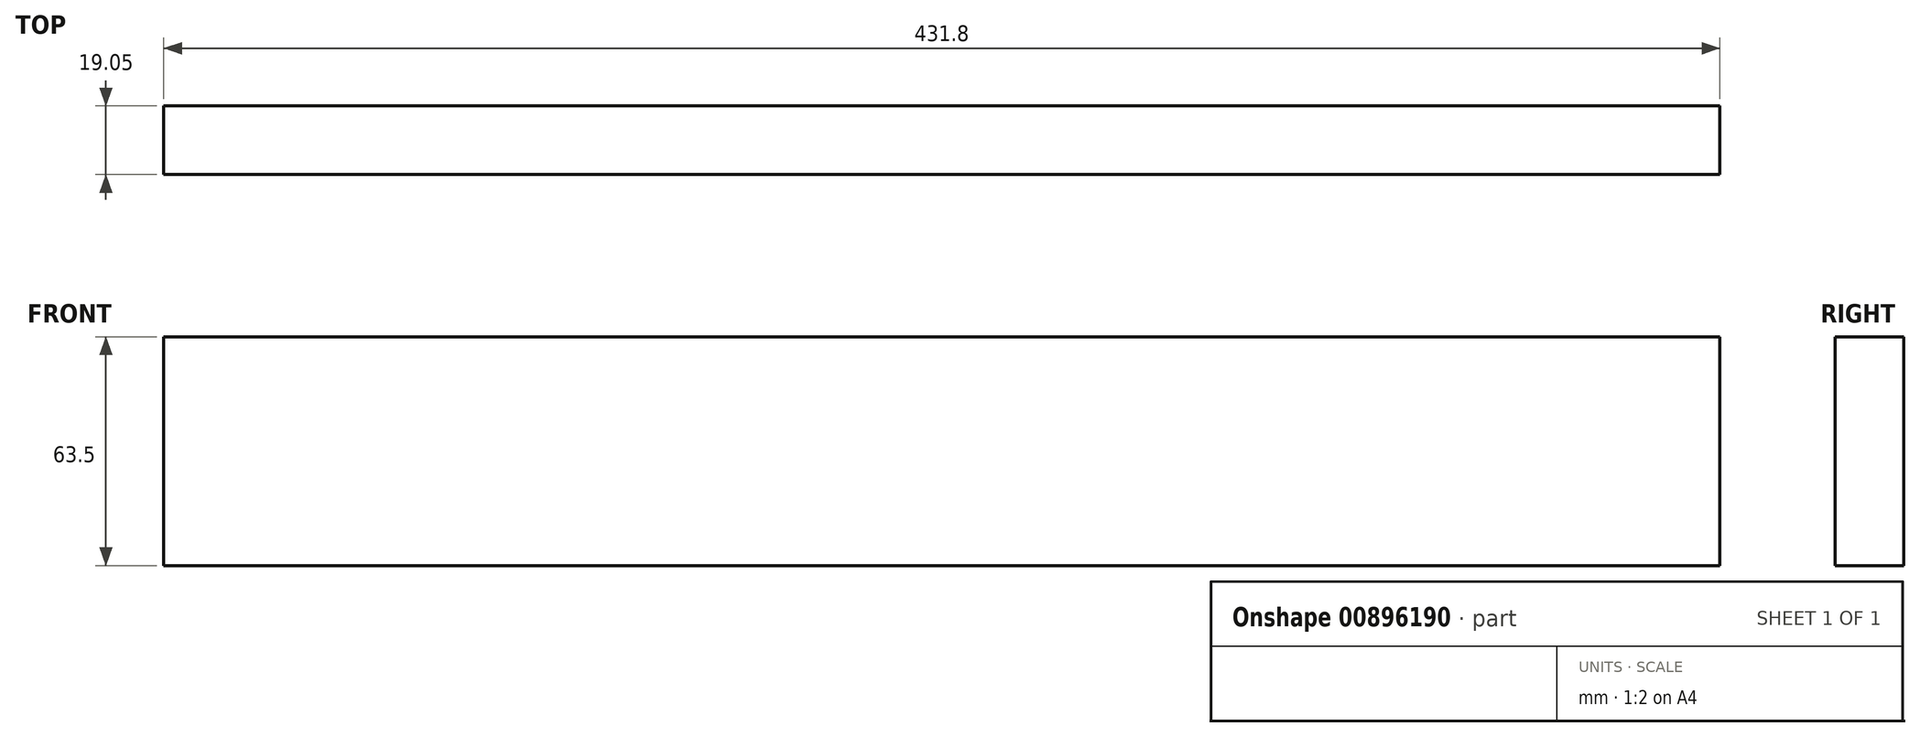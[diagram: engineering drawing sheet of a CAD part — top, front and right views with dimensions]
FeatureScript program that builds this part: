
annotation { "Feature Type Name" : "Feature", "Feature Type Description" : "" }
export const myFeature = defineFeature(function(context is Context, id is Id, definition is map)
    precondition{}
    {
        {
            var Q0;
            Q0=qCreatedBy(makeId("Front.planeOp"),FACE);
            var sketch = newSketch(context, id + "F0", { "sketchPlane" : qUnion([Q0])});
            skLineSegment(sketch, "E0.bottom", {"start": v(0, 0) * mm, "end": v(431.8, 0) * mm});
            skLineSegment(sketch, "E0.top", {"start": v(0, -63.5) * mm, "end": v(431.8, -63.5) * mm});
            skLineSegment(sketch, "E0.left", {"start": v(0, 0) * mm, "end": v(0, -63.5) * mm});
            skLineSegment(sketch, "E0.right", {"start": v(431.8, 0) * mm, "end": v(431.8, -63.5) * mm});
            skSolve(sketch);
        }
        {
            var Q0;
            Q0=makeQuery(id+"F0.imprint","IMPRINT",FACE,{"disambiguationData":[TD([[makeQuery(id+"F0.imprint","IMPRINT",EDGE,{"derivedFrom":sQuery(id+"F0.wireOp",EDGE,"E0.bottom")}),-1.0]])]});
            extrude(context, id + "F1", {"entities" : qUnion([Q0]), "depth" : 19.05 * mm, "offsetDistance" : 25.4 * mm});
        }
    });
